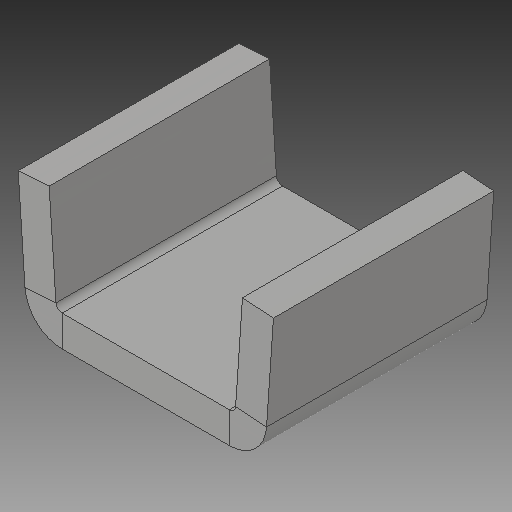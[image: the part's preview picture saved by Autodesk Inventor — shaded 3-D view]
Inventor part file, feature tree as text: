
AUTODESK INVENTOR PART (.ipt)
format: ipt  version: 2018 (Build 220112000, 112)  size: 119,296 bytes
history: native  units: mm
features: sheet_metal_op x4, sketch x2, other x2
ambient origin geometry x8: Origin, YZ Plane, XZ Plane, XY Plane, X Axis, Y Axis, Z Axis, Center Point
bodies: Solid1 (feature_tree)
feature tree (8):
  sheet_metal_op  "Face1"
  sheet_metal_op  "Flange1"
  sketch  "Sketch1"  dims[d0=35.5mm]
  other  "Plate1"
  sketch  "Sketch2"  dims[d1=5.0mm d2=5.0mm d3=2.5mm d4=10.0mm d5=1.0mm d6=21.37mm d7=15.009832mm d8=1.0mm d9=20.0mm d10=5.0mm d11=1.0mm d12=38.128mm]
  other  "Plate2"
  sheet_metal_op  "Bend1"
  sheet_metal_op  "Corner1"
